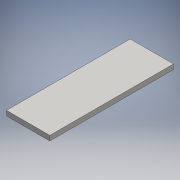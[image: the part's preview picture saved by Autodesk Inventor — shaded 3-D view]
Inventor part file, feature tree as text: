
AUTODESK INVENTOR PART (.ipt)
format: ipt  version: 2016 SP1 (Build 200210100, 210)  size: 88,064 bytes
history: native  units: mm
features: extrude x1, sketch x1
ambient origin geometry x8: Origin, YZ Plane, XZ Plane, XY Plane, X Axis, Y Axis, Z Axis, Center Point
bodies: Solid1 (feature_tree)
feature tree (2):
  extrude  "Extrusion1"  Depth=200.0mm
  sketch  "Sketch1"  dims[d0=70.0mm d1=200.0mm d2=100.0mm d3=35.0mm d4=8.0mm d5=0.0mm]
